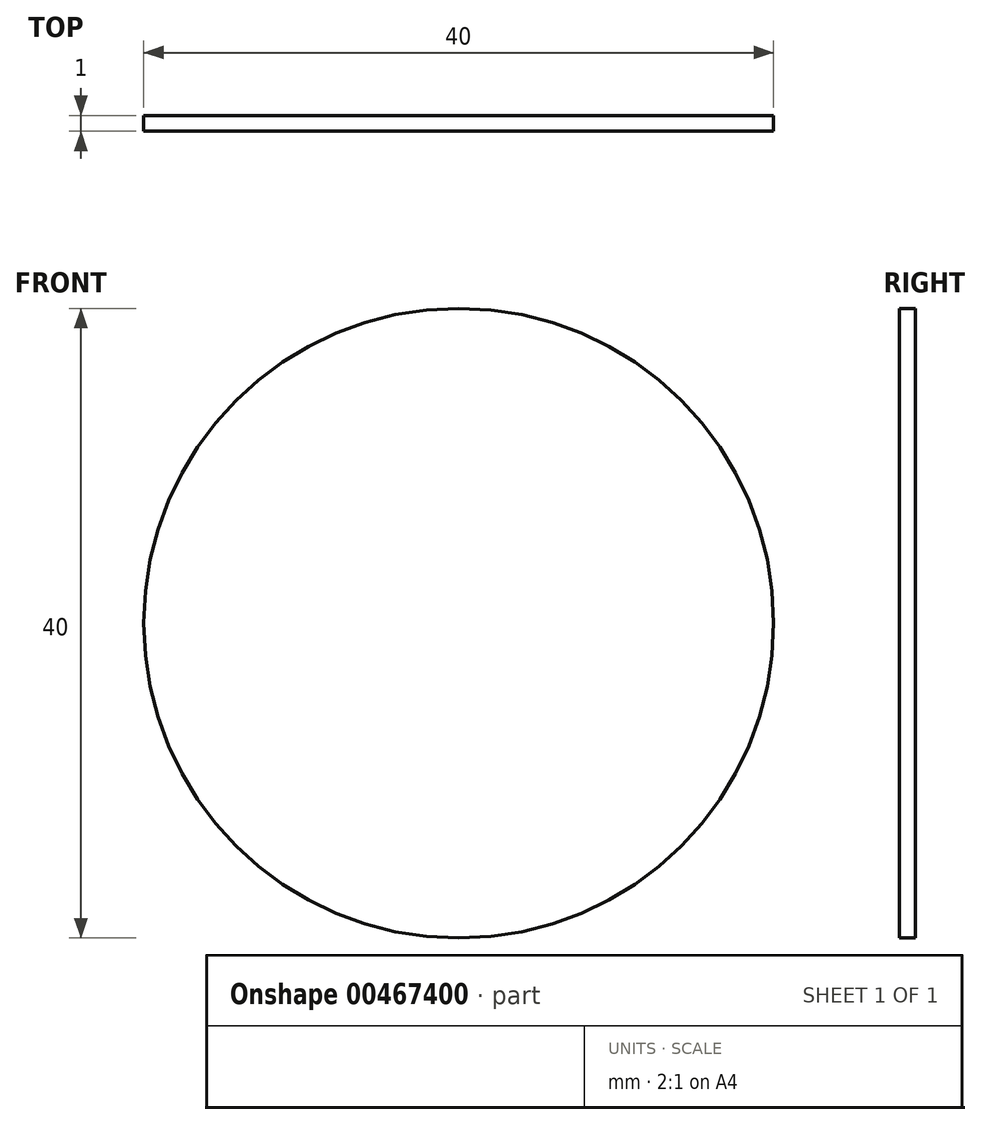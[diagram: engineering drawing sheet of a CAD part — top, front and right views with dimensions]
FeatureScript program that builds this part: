
annotation { "Feature Type Name" : "Feature", "Feature Type Description" : "" }
export const myFeature = defineFeature(function(context is Context, id is Id, definition is map)
    precondition{}
    {
        {
            var Q0;
            Q0=qCreatedBy(makeId("Front.planeOp"),FACE);
            var sketch = newSketch(context, id + "F0", { "sketchPlane" : qUnion([Q0])});
            skCircle(sketch, "E0", {"center": v(0, 0) * mm, "radius": 20 * mm});
            skSolve(sketch);
        }
        {
            var Q0;
            Q0=makeQuery(id+"F0.imprint","IMPRINT",FACE,{"disambiguationData":[TD([[makeQuery(id+"F0.imprint","IMPRINT",EDGE,{"derivedFrom":sQuery(id+"F0.wireOp",EDGE,"E0")}),1.0]])]});
            extrude(context, id + "F1", {"entities" : qUnion([Q0]), "depth" : 1 * mm, "offsetDistance" : 25 * mm});
        }
    });
